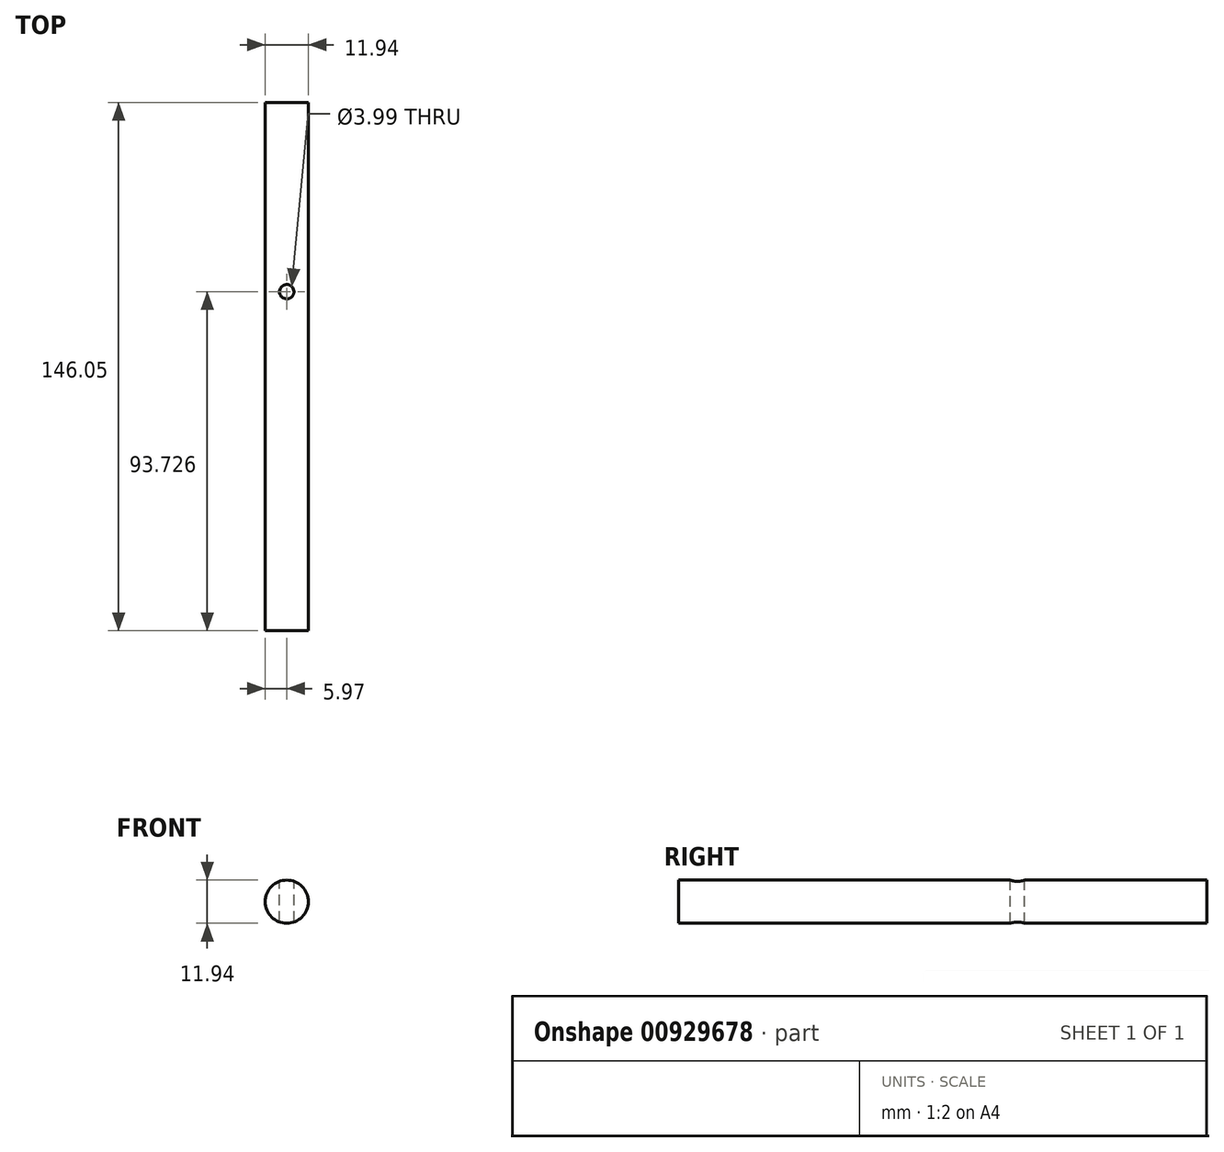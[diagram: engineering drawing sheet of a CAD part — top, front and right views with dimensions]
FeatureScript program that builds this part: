
annotation { "Feature Type Name" : "Feature", "Feature Type Description" : "" }
export const myFeature = defineFeature(function(context is Context, id is Id, definition is map)
    precondition{}
    {
        {
            var Q0;
            Q0=qCreatedBy(makeId("Front.planeOp"),FACE);
            var sketch = newSketch(context, id + "F0", { "sketchPlane" : qUnion([Q0])});
            skCircle(sketch, "E0", {"center": v(0, 0) * mm, "radius": 5.97 * mm});
            skSolve(sketch);
        }
        {
            var Q0;
            Q0=makeQuery(id+"F0.imprint","IMPRINT",FACE,{"disambiguationData":[TD([[makeQuery(id+"F0.imprint","IMPRINT",EDGE,{"derivedFrom":sQuery(id+"F0.wireOp",EDGE,"E0")}),1.0]])]});
            extrude(context, id + "F1", {"entities" : qUnion([Q0]), "depth" : 146.05 * mm, "offsetDistance" : 25.4 * mm});
        }
        {
            var Q0;
            Q0=qCreatedBy(makeId("Top.planeOp"),FACE);
            var sketch = newSketch(context, id + "F2", { "sketchPlane" : qUnion([Q0])});
            skCircle(sketch, "E1", {"center": v(0, -52.32) * mm, "radius": 2 * mm});
            skSolve(sketch);
        }
        {
            var Q0;
            Q0 = qSketchRegion(id + "F2", true);
            extrude(context, id + "F3", {"entities" : qUnion([Q0]), "operationType" : NewBodyOperationType.REMOVE, "endBound" : BoundingType.SYMMETRIC, "oppositeDirection" : true, "depth" : 25.4 * mm, "offsetDistance" : 25.4 * mm});
        }
    });
